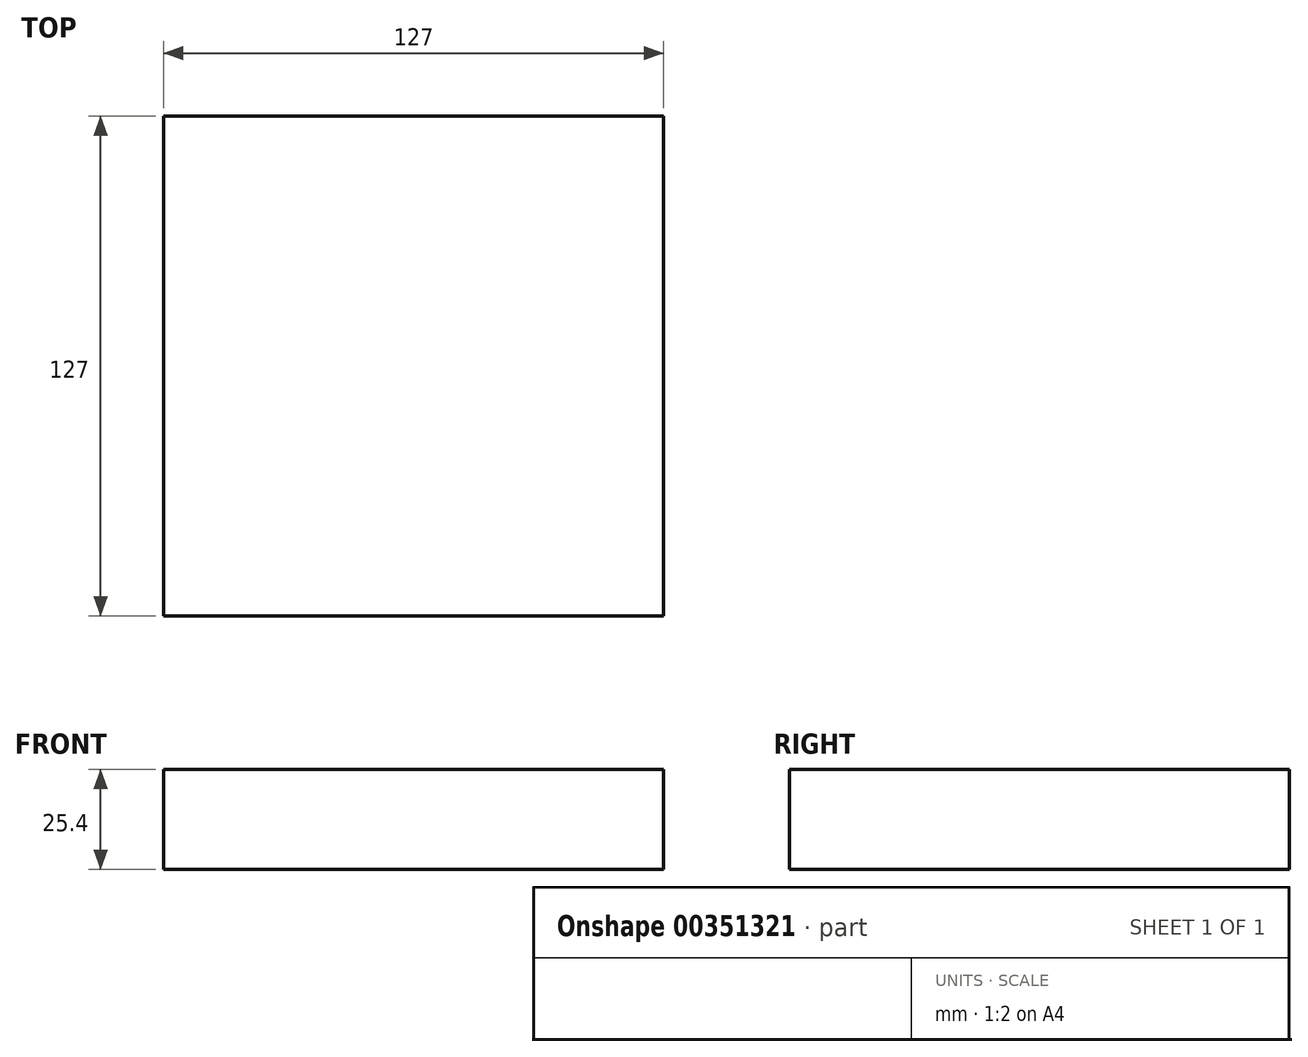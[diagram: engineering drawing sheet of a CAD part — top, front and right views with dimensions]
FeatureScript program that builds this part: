
annotation { "Feature Type Name" : "Feature", "Feature Type Description" : "" }
export const myFeature = defineFeature(function(context is Context, id is Id, definition is map)
    precondition{}
    {
        {
            var Q0;
            Q0=qCreatedBy(makeId("Top.planeOp"),FACE);
            var sketch = newSketch(context, id + "F0", { "sketchPlane" : qUnion([Q0])});
            skLineSegment(sketch, "E0.bottom", {"start": v(63.5, -63.5) * mm, "end": v(-63.5, -63.5) * mm});
            skLineSegment(sketch, "E0.top", {"start": v(63.5, 63.5) * mm, "end": v(-63.5, 63.5) * mm});
            skLineSegment(sketch, "E0.left", {"start": v(63.5, -63.5) * mm, "end": v(63.5, 63.5) * mm});
            skLineSegment(sketch, "E0.right", {"start": v(-63.5, -63.5) * mm, "end": v(-63.5, 63.5) * mm});
            skPoint(sketch, "E0.middle", {"position": v(0, 0) * mm});
            skSolve(sketch);
        }
        {
            var Q0;
            Q0 = qSketchRegion(id + "F0", true);
            extrude(context, id + "F1", {"entities" : qUnion([Q0]), "depth" : 25.4 * mm});
        }
    });
